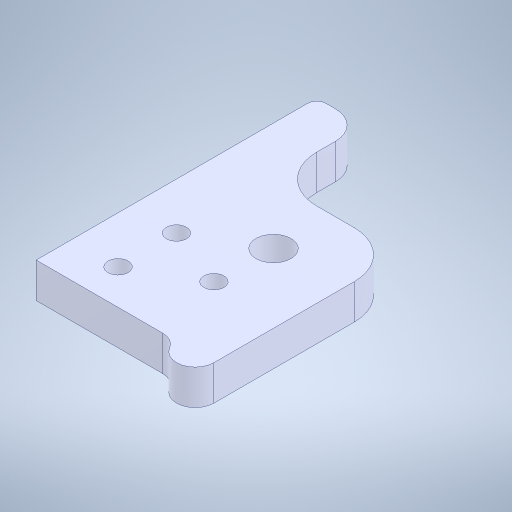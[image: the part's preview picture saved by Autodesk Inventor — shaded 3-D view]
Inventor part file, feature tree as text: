
AUTODESK INVENTOR PART (.ipt)
format: ipt  version: 2023.2 (Build 272271000, 271)  size: 251,392 bytes
history: mixed  units: in
note: dims shown in document units (in); Inventor stores cm internally (conversion verified against a paired STEP export)
features: fillet x1, imported_body x1
ambient origin geometry x8: Origin, YZ Plane, XZ Plane, XY Plane, X Axis, Y Axis, Z Axis, Center Point
bodies: Solid1 (imported_parasolid)
feature tree (2):
  fillet  "Fillet1"  [1 undecoded]
  imported_body  NMx_Import_Brep_tag  [imported B-rep: ~24 faces, bbox_mm=[48.26, 9.525, 78.74]]
note: 1 required parameter value undecoded (feature->parameter linkage not recoverable at this tier; creation-order binding heuristic only, values carry confidence <= 0.55)
